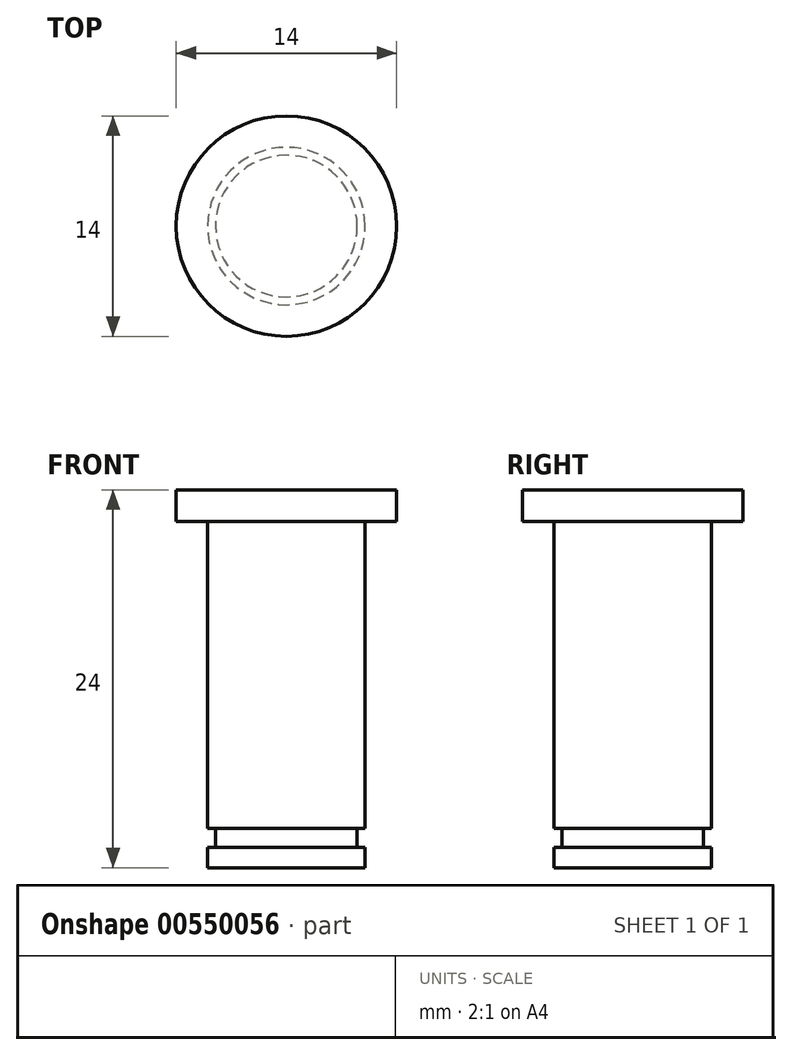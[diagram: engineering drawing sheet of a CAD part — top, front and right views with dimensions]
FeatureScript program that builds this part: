
annotation { "Feature Type Name" : "Feature", "Feature Type Description" : "" }
export const myFeature = defineFeature(function(context is Context, id is Id, definition is map)
    precondition{}
    {
        {
            var Q0;
            Q0=qCreatedBy(makeId("Front.planeOp"),FACE);
            var sketch = newSketch(context, id + "F0", { "sketchPlane" : qUnion([Q0])});
            skLineSegment(sketch, "E0", {"start": v(0, 0) * mm, "end": v(0, 28.19) * mm, "construction": true});
            skLineSegment(sketch, "E1", {"start": v(0, 0) * mm, "end": v(5, 0) * mm});
            skLineSegment(sketch, "E2", {"start": v(5, 0) * mm, "end": v(5, 1.3) * mm});
            skLineSegment(sketch, "E3", {"start": v(5, 1.3) * mm, "end": v(4.5, 1.3) * mm});
            skLineSegment(sketch, "E4", {"start": v(4.5, 1.3) * mm, "end": v(4.5, 2.5) * mm});
            skLineSegment(sketch, "E5", {"start": v(4.5, 2.5) * mm, "end": v(5, 2.5) * mm});
            skLineSegment(sketch, "E6", {"start": v(5, 2.5) * mm, "end": v(5, 22) * mm});
            skLineSegment(sketch, "E7", {"start": v(5, 22) * mm, "end": v(7, 22) * mm});
            skLineSegment(sketch, "E8", {"start": v(7, 22) * mm, "end": v(7, 24) * mm});
            skLineSegment(sketch, "E9", {"start": v(7, 24) * mm, "end": v(0, 24) * mm});
            skLineSegment(sketch, "E10", {"start": v(0, 24) * mm, "end": v(0, 0) * mm});
            skSolve(sketch);
        }
        {
            var Q0;
            Q0=makeQuery(id+"F0.imprint","IMPRINT",FACE,{"disambiguationData":[TD([[makeQuery(id+"F0.imprint","IMPRINT",EDGE,{"derivedFrom":sQuery(id+"F0.wireOp",EDGE,"E1")}),1.0]])]});
            var Q1;
            Q1=sQuery(id+"F0.wireOp",EDGE,"E0");
            revolve(context, id + "F1", {"surfaceOperationType" : NewSurfaceOperationType.NEW, "entities" : qUnion([Q0]), "axis" : qUnion([Q1]), "revolveType" : RevolveType.FULL});
        }
    });
